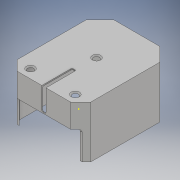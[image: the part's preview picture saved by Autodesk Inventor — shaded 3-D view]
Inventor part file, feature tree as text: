
AUTODESK INVENTOR PART (.ipt)
format: ipt  version: 2017 (Build 210142000, 142)  size: 281,088 bytes
history: native  units: mm
features: sketch x11, extrude x10, other x5, fillet x4, hole x3, projected_geometry x1
ambient origin geometry x8: Origin, YZ Plane, XZ Plane, XY Plane, X Axis, Y Axis, Z Axis, Center Point
bodies: Body1 (feature_tree)
feature tree (34):
  other  "Твердое тело1"
  sketch  "Эскиз1"
  extrude  "Выдавливание1"  Depth=60.0mm
  extrude  "Выдавливание2"  Depth=77.0mm
  fillet  "Сопряжение1"  Radius=11.0mm
  extrude  "Выдавливание3"  Depth=11.0mm
  extrude  "Выдавливание4"  Depth=8.5mm
  extrude  "Выдавливание5"  Depth=8.5mm
  other  "Комбинировать1"
  hole  "Отверстие4"  [1 undecoded]
  hole  "Отверстие5"  [1 undecoded]
  hole  "Отверстие6"  [1 undecoded]
  fillet  "Сопряжение2"  Radius=11.0mm
  fillet  "Сопряжение3"  Radius=1.2mm
  extrude  "Выдавливание6"  Depth=1.0mm TaperAngle=0.0deg
  extrude  "Выдавливание7"  Depth=43.0mm TaperAngle=0.0deg
  extrude  "Выдавливание8"  Depth=1.0mm
  other  "Комбинировать2"
  fillet  "Сопряжение4"  Radius=3.5mm
  extrude  "Выдавливание9"  Depth=25.0mm
  sketch  "Эскиз8"
  sketch  "Эскиз9"
  sketch  "Эскиз10"
  extrude  "Выдавливание10"  Depth=18.0mm TaperAngle=0.0deg
  other  "Твердое тело2"
  sketch  "Эскиз2"
  sketch  "Эскиз3"
  sketch  "Эскиз4"
  other  "Твердое тело3"
  sketch  "Эскиз5"
  sketch  "Эскиз6"
  sketch  "Эскиз7"
  sketch  "Эскиз11"
  projected_geometry  "Спроецированная петля1"
note: 3 required parameter values undecoded (feature->parameter linkage not recoverable at this tier; creation-order binding heuristic only, values carry confidence <= 0.55)
